annotation { "Feature Type Name" : "Feature", "Feature Type Description" : "" }
export const myFeature = defineFeature(function(context is Context, id is Id, definition is map)
    precondition{}
    {
        {
            var Q0;
            Q0=qCreatedBy(makeId("Front.planeOp"),FACE);
            var sketch = newSketch(context, id + "F0", { "sketchPlane" : qUnion([Q0])});
            skLineSegment(sketch, "E0", {"start": v(0, 0) * mm, "end": v(381, 0) * mm});
            skLineSegment(sketch, "E1", {"start": v(0, 0) * mm, "end": v(-381, 0) * mm});
            skLineSegment(sketch, "E2", {"start": v(0, 0) * mm, "end": v(0, 190.5) * mm, "construction": true});
            skLineSegment(sketch, "E3", {"start": v(-381, 0) * mm, "end": v(0, 190.5) * mm});
            skLineSegment(sketch, "E4", {"start": v(0, 190.5) * mm, "end": v(381, 0) * mm});
            skLineSegment(sketch, "E5", {"start": v(0, 190.5) * mm, "end": v(0, 228.6) * mm, "construction": true});
            skLineSegment(sketch, "E6", {"start": v(-381, 0) * mm, "end": v(-457.2, 0) * mm});
            skLineSegment(sketch, "E7", {"start": v(381, 0) * mm, "end": v(457.2, 0) * mm});
            skLineSegment(sketch, "E8", {"start": v(457.2, 0) * mm, "end": v(0, 228.6) * mm});
            skLineSegment(sketch, "E9", {"start": v(-457.2, 0) * mm, "end": v(0, 228.6) * mm});
            skLineSegment(sketch, "E10", {"start": v(-381, 0) * mm, "end": v(-381, -279.4) * mm});
            skLineSegment(sketch, "E11", {"start": v(381, 0) * mm, "end": v(381, -279.4) * mm});
            skLineSegment(sketch, "E12", {"start": v(381, -279.4) * mm, "end": v(-381, -279.4) * mm});
            skLineSegment(sketch, "E13", {"start": v(-381, -279.4) * mm, "end": v(-381, -330.2) * mm});
            skLineSegment(sketch, "E14", {"start": v(381, -279.4) * mm, "end": v(381, -330.2) * mm});
            skLineSegment(sketch, "E15", {"start": v(381, -330.2) * mm, "end": v(-381, -330.2) * mm});
            skLineSegment(sketch, "E16", {"start": v(-279.4, -279.4) * mm, "end": v(-279.4, -101.6) * mm});
            skLineSegment(sketch, "E17", {"start": v(-279.4, -101.6) * mm, "end": v(-203.2, -101.6) * mm});
            skLineSegment(sketch, "E18", {"start": v(-203.2, -101.6) * mm, "end": v(-203.2, -279.4) * mm});
            skLineSegment(sketch, "E19", {"start": v(-203.2, -279.4) * mm, "end": v(-279.4, -279.4) * mm});
            skLineSegment(sketch, "E20.0", {"start": v(-177.8, -76.2) * mm, "end": v(-177.8, -279.4) * mm});
            skLineSegment(sketch, "E20.1", {"start": v(-304.8, -76.2) * mm, "end": v(-177.8, -76.2) * mm});
            skLineSegment(sketch, "E20.2", {"start": v(-304.8, -279.4) * mm, "end": v(-304.8, -76.2) * mm});
            skLineSegment(sketch, "E21", {"start": v(-304.8, -279.4) * mm, "end": v(-279.4, -279.4) * mm});
            skLineSegment(sketch, "E22", {"start": v(-203.2, -279.4) * mm, "end": v(-177.8, -279.4) * mm});
            skLineSegment(sketch, "E23", {"start": v(381, -330.2) * mm, "end": v(762, -330.2) * mm});
            skLineSegment(sketch, "E24", {"start": v(381, -279.4) * mm, "end": v(762, -279.4) * mm});
            skLineSegment(sketch, "E25", {"start": v(762, -279.4) * mm, "end": v(762, -330.2) * mm});
            skLineSegment(sketch, "E26", {"start": v(762, -279.4) * mm, "end": v(762, -50.8) * mm});
            skLineSegment(sketch, "E27", {"start": v(381, 0) * mm, "end": v(762, -50.8) * mm});
            skLineSegment(sketch, "E28", {"start": v(762, -101.6) * mm, "end": v(381, -50.8) * mm});
            skLineSegment(sketch, "E29.bottom", {"start": v(50.8, -101.6) * mm, "end": v(279.4, -101.6) * mm});
            skLineSegment(sketch, "E29.top", {"start": v(50.8, -203.2) * mm, "end": v(279.4, -203.2) * mm});
            skLineSegment(sketch, "E29.left", {"start": v(50.8, -101.6) * mm, "end": v(50.8, -203.2) * mm});
            skLineSegment(sketch, "E29.right", {"start": v(279.4, -101.6) * mm, "end": v(279.4, -203.2) * mm});
            skLineSegment(sketch, "E30.0", {"start": v(38.1, -88.9) * mm, "end": v(292.1, -88.9) * mm});
            skLineSegment(sketch, "E30.1", {"start": v(38.1, -88.9) * mm, "end": v(38.1, -215.9) * mm});
            skLineSegment(sketch, "E30.2", {"start": v(38.1, -215.9) * mm, "end": v(292.1, -215.9) * mm});
            skLineSegment(sketch, "E30.3", {"start": v(292.1, -88.9) * mm, "end": v(292.1, -215.9) * mm});
            skLineSegment(sketch, "E31.bottom", {"start": v(508, -127) * mm, "end": v(596.9, -127) * mm});
            skLineSegment(sketch, "E31.top", {"start": v(508, -228.6) * mm, "end": v(596.9, -228.6) * mm});
            skLineSegment(sketch, "E31.left", {"start": v(508, -127) * mm, "end": v(508, -228.6) * mm});
            skLineSegment(sketch, "E31.right", {"start": v(596.9, -127) * mm, "end": v(596.9, -228.6) * mm});
            skLineSegment(sketch, "E32.0", {"start": v(495.3, -114.3) * mm, "end": v(609.6, -114.3) * mm});
            skLineSegment(sketch, "E32.1", {"start": v(495.3, -114.3) * mm, "end": v(495.3, -241.3) * mm});
            skLineSegment(sketch, "E32.2", {"start": v(495.3, -241.3) * mm, "end": v(609.6, -241.3) * mm});
            skLineSegment(sketch, "E32.3", {"start": v(609.6, -114.3) * mm, "end": v(609.6, -241.3) * mm});
            skText(sketch, "E33", { "text": "Property of\nLily Preston", "fontName": "OpenSans-Regular.ttf"});
            skLineSegment(sketch, "E34", {"start": v(246.7, 105.25) * mm, "end": v(246.7, 232.25) * mm});
            skLineSegment(sketch, "E35", {"start": v(246.7, 232.25) * mm, "end": v(170.5, 232.25) * mm});
            skLineSegment(sketch, "E36", {"start": v(170.5, 232.25) * mm, "end": v(170.5, 143.35) * mm});
            skLineSegment(sketch, "E37", {"start": v(170.5, 143.35) * mm, "end": v(246.7, 105.25) * mm});
            const initialGuessF0  = {"E33": [0.4505, 0.09872, 1, 0, 0.02776]};
            skSetInitialGuess(sketch, initialGuessF0);
            skSolve(sketch);
        }
        {
            var Q0;
            Q0=makeQuery(id+"F0.imprint","IMPRINT",FACE,{"disambiguationData":[TD([[makeQuery(id+"F0.imprint","IMPRINT",EDGE,{"derivedFrom":sQuery(id+"F0.wireOp",EDGE,"E3")}),1.0]])]});
            var Q1;
            {var subQ0=sQuery(id+"F0.wireOp",EDGE,"E27");Q1=makeQuery(id+"F0.imprint","IMPRINT",FACE,{"disambiguationData":[TD([[makeQuery(id+"F0.imprint","IMPRINT",EDGE,{"derivedFrom":subQ0}),-1.0]])]});}
            extrude(context, id + "F1", {"entities" : qUnion([Q0, Q1]), "depth" : 76.2 * mm, "offsetDistance" : 25.4 * mm, "hasSecondDirection" : true, "secondDirectionOppositeDirection" : true, "secondDirectionDepth" : 1016 * mm});
        }
        {
            var Q0;
            Q0=makeQuery(id+"F0.imprint","IMPRINT",FACE,{"disambiguationData":[TD([[makeQuery(id+"F0.imprint","IMPRINT",EDGE,{"derivedFrom":sQuery(id+"F0.wireOp",EDGE,"E0")}),1.0]])]});
            extrude(context, id + "F2", {"entities" : qUnion([Q0]), "operationType" : NewBodyOperationType.ADD, "depth" : 38.1 * mm, "offsetDistance" : 25.4 * mm, "hasSecondDirection" : true, "secondDirectionOppositeDirection" : true, "secondDirectionDepth" : 990.6 * mm});
        }
        {
            var Q0;
            {var subQ6=sQuery(id+"F0.wireOp",EDGE,"E0");Q0=makeQuery(id+"F0.imprint","IMPRINT",FACE,{"disambiguationData":[TD([[makeQuery(id+"F0.imprint","IMPRINT",EDGE,{"derivedFrom":subQ6}),-1.0]])]});}
            var Q1;
            {var subQ1=sQuery(id+"F0.wireOp",EDGE,"E24");Q1=makeQuery(id+"F0.imprint","IMPRINT",FACE,{"disambiguationData":[TD([[makeQuery(id+"F0.imprint","IMPRINT",EDGE,{"derivedFrom":subQ1}),1.0]])]});}
            extrude(context, id + "F3", {"entities" : qUnion([Q0, Q1]), "depth" : 38.1 * mm, "offsetDistance" : 25.4 * mm, "hasSecondDirection" : true, "secondDirectionOppositeDirection" : true, "secondDirectionDepth" : 990.6 * mm});
        }
        {
            var Q0;
            Q0=makeQuery(id+"F0.imprint","IMPRINT",FACE,{"disambiguationData":[TD([[makeQuery(id+"F0.imprint","IMPRINT",EDGE,{"derivedFrom":sQuery(id+"F0.wireOp",EDGE,"E16")}),1.0]])]});
            var Q1;
            Q1=makeQuery(id+"F0.imprint","IMPRINT",FACE,{"disambiguationData":[TD([[makeQuery(id+"F0.imprint","IMPRINT",EDGE,{"derivedFrom":sQuery(id+"F0.wireOp",EDGE,"E29.bottom")}),1.0]])]});
            var Q2;
            Q2=makeQuery(id+"F0.imprint","IMPRINT",FACE,{"disambiguationData":[TD([[makeQuery(id+"F0.imprint","IMPRINT",EDGE,{"derivedFrom":sQuery(id+"F0.wireOp",EDGE,"E31.bottom")}),1.0]])]});
            extrude(context, id + "F4", {"entities" : qUnion([Q0, Q1, Q2]), "operationType" : NewBodyOperationType.ADD, "depth" : 50.8 * mm, "offsetDistance" : 25.4 * mm, "hasSecondDirection" : true, "secondDirectionOppositeDirection" : true, "secondDirectionDepth" : 990.6 * mm});
        }
        {
            var Q0;
            Q0=makeQuery(id+"F0.imprint","IMPRINT",FACE,{"disambiguationData":[TD([[makeQuery(id+"F0.imprint","IMPRINT",EDGE,{"derivedFrom":sQuery(id+"F0.wireOp",EDGE,"E16")}),-1.0]])]});
            var Q1;
            Q1=makeQuery(id+"F0.imprint","IMPRINT",FACE,{"disambiguationData":[TD([[makeQuery(id+"F0.imprint","IMPRINT",EDGE,{"derivedFrom":sQuery(id+"F0.wireOp",EDGE,"E29.bottom")}),-1.0]])]});
            var Q2;
            Q2=makeQuery(id+"F0.imprint","IMPRINT",FACE,{"disambiguationData":[TD([[makeQuery(id+"F0.imprint","IMPRINT",EDGE,{"derivedFrom":sQuery(id+"F0.wireOp",EDGE,"E31.bottom")}),-1.0]])]});
            extrude(context, id + "F5", {"entities" : qUnion([Q0, Q1, Q2]), "operationType" : NewBodyOperationType.ADD, "depth" : 38.1 * mm, "offsetDistance" : 25.4 * mm, "hasSecondDirection" : true, "secondDirectionOppositeDirection" : true, "secondDirectionDepth" : 990.6 * mm});
        }
        {
            var Q0;
            {var subQ1=sQuery(id+"F0.wireOp",EDGE,"E13");Q0=makeQuery(id+"F0.imprint","IMPRINT",FACE,{"disambiguationData":[TD([[makeQuery(id+"F0.imprint","IMPRINT",EDGE,{"derivedFrom":subQ1}),1.0]])]});}
            var Q1;
            Q1=makeQuery(id+"F0.imprint","IMPRINT",FACE,{"disambiguationData":[TD([[makeQuery(id+"F0.imprint","IMPRINT",EDGE,{"derivedFrom":sQuery(id+"F0.wireOp",EDGE,"E14")}),1.0]])]});
            extrude(context, id + "F6", {"entities" : qUnion([Q0, Q1]), "operationType" : NewBodyOperationType.ADD, "depth" : 381 * mm, "offsetDistance" : 25.4 * mm, "hasSecondDirection" : true, "secondDirectionOppositeDirection" : true, "secondDirectionDepth" : 990.6 * mm});
        }
        {
            var Q0;
            Q0=makeQuery(id+"F6.opExtrude","CAP_EDGE",EDGE,{"disambiguationData":[OSD([sQuery(id+"F0.wireOp",EDGE,"E12"),sQuery(id+"F0.wireOp",EDGE,"E19"),sQuery(id+"F0.wireOp",EDGE,"E21"),sQuery(id+"F0.wireOp",EDGE,"E22"),sQuery(id+"F0.wireOp",EDGE,"E24")])],"isStart":false});
            fillet(context, id + "F7", {"entities" : qUnion([Q0]), "radius" : 76.2 * mm, "tangentPropagation" : true, "allowEdgeOverflow" : false});
        }
        {
            var Q0;
            Q0=makeQuery(id+"F6.opExtrude","SWEPT_FACE",FACE,{"disambiguationData":[OSD([sQuery(id+"F0.wireOp",EDGE,"E12"),sQuery(id+"F0.wireOp",EDGE,"E19"),sQuery(id+"F0.wireOp",EDGE,"E21"),sQuery(id+"F0.wireOp",EDGE,"E22"),sQuery(id+"F0.wireOp",EDGE,"E24")])]});
            var sketch = newSketch(context, id + "F8", { "sketchPlane" : qUnion([Q0])});
            skText(sketch, "E38", { "text": "Lily Preston\n", "fontName": "OpenSans-Regular.ttf"});
            const initialGuessF8  = {"E38": [-0.21851, -0.22048, 1, 0, 0.09562]};
            skSetInitialGuess(sketch, initialGuessF8);
            skSolve(sketch);
        }
        {
            var Q0;
            Q0 = qSketchRegion(id + "F8", true);
            extrude(context, id + "F9", {"entities" : qUnion([Q0]), "operationType" : NewBodyOperationType.ADD, "depth" : 12.7 * mm, "offsetDistance" : 25.4 * mm});
        }
        {
            var Q0;
            Q0=makeQuery(id+"F6.boolean.opBoolean","MERGE",FACE,{"derivedFrom":[makeQuery(id+"F3.opExtrude","SWEPT_FACE",FACE,{"disambiguationData":[OSD([sQuery(id+"F0.wireOp",EDGE,"E26")])]}),makeQuery(id+"F6.opExtrude","SWEPT_FACE",FACE,{"disambiguationData":[OSD([sQuery(id+"F0.wireOp",EDGE,"E25")])]})]});
            var sketch = newSketch(context, id + "F10", { "sketchPlane" : qUnion([Q0])});
            skLineSegment(sketch, "E39.bottom", {"start": v(139.7, -177.8) * mm, "end": v(266.7, -177.8) * mm});
            skLineSegment(sketch, "E39.top", {"start": v(139.7, -254) * mm, "end": v(266.7, -254) * mm});
            skLineSegment(sketch, "E39.left", {"start": v(139.7, -177.8) * mm, "end": v(139.7, -254) * mm});
            skLineSegment(sketch, "E39.right", {"start": v(266.7, -177.8) * mm, "end": v(266.7, -254) * mm});
            skLineSegment(sketch, "E40.0", {"start": v(114.3, -152.4) * mm, "end": v(292.1, -152.4) * mm});
            skLineSegment(sketch, "E40.1", {"start": v(114.3, -152.4) * mm, "end": v(114.3, -279.4) * mm});
            skLineSegment(sketch, "E40.2", {"start": v(114.3, -279.4) * mm, "end": v(292.1, -279.4) * mm});
            skLineSegment(sketch, "E40.3", {"start": v(292.1, -152.4) * mm, "end": v(292.1, -279.4) * mm});
            skLineSegment(sketch, "E41.bottom", {"start": v(685.8, -177.8) * mm, "end": v(812.8, -177.8) * mm});
            skLineSegment(sketch, "E41.top", {"start": v(685.8, -254) * mm, "end": v(812.8, -254) * mm});
            skLineSegment(sketch, "E41.left", {"start": v(685.8, -177.8) * mm, "end": v(685.8, -254) * mm});
            skLineSegment(sketch, "E41.right", {"start": v(812.8, -177.8) * mm, "end": v(812.8, -254) * mm});
            skLineSegment(sketch, "E42.0", {"start": v(660.4, -152.4) * mm, "end": v(838.2, -152.4) * mm});
            skLineSegment(sketch, "E42.1", {"start": v(660.4, -152.4) * mm, "end": v(660.4, -279.4) * mm});
            skLineSegment(sketch, "E42.2", {"start": v(660.4, -279.4) * mm, "end": v(838.2, -279.4) * mm});
            skLineSegment(sketch, "E42.3", {"start": v(838.2, -152.4) * mm, "end": v(838.2, -279.4) * mm});
            skSolve(sketch);
        }
        {
            var Q0;
            Q0=makeQuery(id+"F10.imprint","IMPRINT",FACE,{"disambiguationData":[TD([[makeQuery(id+"F10.imprint","IMPRINT",EDGE,{"derivedFrom":sQuery(id+"F10.wireOp",EDGE,"E39.bottom")}),1.0]])]});
            var Q1;
            Q1=makeQuery(id+"F10.imprint","IMPRINT",FACE,{"disambiguationData":[TD([[makeQuery(id+"F10.imprint","IMPRINT",EDGE,{"derivedFrom":sQuery(id+"F10.wireOp",EDGE,"E41.bottom")}),1.0]])]});
            extrude(context, id + "F11", {"entities" : qUnion([Q0, Q1]), "operationType" : NewBodyOperationType.ADD, "depth" : 20.32 * mm, "offsetDistance" : 25.4 * mm});
        }
        {
            var Q0;
            Q0=makeQuery(id+"F11.boolean.opBoolean","SPLIT",FACE,{"disambiguationData":[TD([makeQuery(id+"F11.opExtrude","SWEPT_FACE",FACE,{"disambiguationData":[OSD([sQuery(id+"F10.wireOp",EDGE,"E39.bottom")])]})])],"derivedFrom":makeQuery(id+"F6.boolean.opBoolean","MERGE",FACE,{"derivedFrom":[makeQuery(id+"F3.opExtrude","SWEPT_FACE",FACE,{"disambiguationData":[OSD([sQuery(id+"F0.wireOp",EDGE,"E26")])]}),makeQuery(id+"F6.opExtrude","SWEPT_FACE",FACE,{"disambiguationData":[OSD([sQuery(id+"F0.wireOp",EDGE,"E25")])]})]})});
            var Q1;
            Q1=makeQuery(id+"F11.boolean.opBoolean","SPLIT",FACE,{"disambiguationData":[TD([makeQuery(id+"F11.opExtrude","SWEPT_FACE",FACE,{"disambiguationData":[OSD([sQuery(id+"F10.wireOp",EDGE,"E41.bottom")])]})])],"derivedFrom":makeQuery(id+"F6.boolean.opBoolean","MERGE",FACE,{"derivedFrom":[makeQuery(id+"F3.opExtrude","SWEPT_FACE",FACE,{"disambiguationData":[OSD([sQuery(id+"F0.wireOp",EDGE,"E26")])]}),makeQuery(id+"F6.opExtrude","SWEPT_FACE",FACE,{"disambiguationData":[OSD([sQuery(id+"F0.wireOp",EDGE,"E25")])]})]})});
            extrude(context, id + "F12", {"entities" : qUnion([Q0, Q1]), "operationType" : NewBodyOperationType.ADD, "depth" : 12.7 * mm, "offsetDistance" : 25.4 * mm});
        }
        {
            var Q0;
            {var subQ0=sQuery(id+"F0.wireOp",EDGE,"E24");var subQ1=sQuery(id+"F0.wireOp",EDGE,"E22");var subQ2=sQuery(id+"F0.wireOp",EDGE,"E21");var subQ3=sQuery(id+"F0.wireOp",EDGE,"E19");var subQ4=sQuery(id+"F0.wireOp",EDGE,"E12");var subQ5=sQuery(id+"F0.wireOp",EDGE,"E31.right");var subQ6=sQuery(id+"F0.wireOp",EDGE,"E31.left");var subQ7=sQuery(id+"F0.wireOp",EDGE,"E31.top");var subQ8=sQuery(id+"F0.wireOp",EDGE,"E31.bottom");var subQ9=sQuery(id+"F0.wireOp",EDGE,"E29.right");var subQ10=sQuery(id+"F0.wireOp",EDGE,"E29.left");var subQ11=sQuery(id+"F0.wireOp",EDGE,"E29.top");var subQ12=sQuery(id+"F0.wireOp",EDGE,"E29.bottom");var subQ13=sQuery(id+"F0.wireOp",EDGE,"E18");var subQ14=sQuery(id+"F0.wireOp",EDGE,"E17");var subQ15=sQuery(id+"F0.wireOp",EDGE,"E16");var subQ16=sQuery(id+"F0.wireOp",EDGE,"E32.3");var subQ17=sQuery(id+"F0.wireOp",EDGE,"E32.2");var subQ18=sQuery(id+"F0.wireOp",EDGE,"E32.1");var subQ19=sQuery(id+"F0.wireOp",EDGE,"E32.0");var subQ20=sQuery(id+"F0.wireOp",EDGE,"E30.3");var subQ21=sQuery(id+"F0.wireOp",EDGE,"E30.2");var subQ22=sQuery(id+"F0.wireOp",EDGE,"E30.1");var subQ23=sQuery(id+"F0.wireOp",EDGE,"E30.0");var subQ24=sQuery(id+"F0.wireOp",EDGE,"E20.2");var subQ25=sQuery(id+"F0.wireOp",EDGE,"E20.1");var subQ26=sQuery(id+"F0.wireOp",EDGE,"E20.0");Q0=makeQuery(id+"F6.boolean.opBoolean","MERGE",FACE,{"derivedFrom":[makeQuery(id+"F5.boolean.opBoolean","MERGE",FACE,{"derivedFrom":[makeQuery(id+"F4.boolean.opBoolean","MERGE",FACE,{"derivedFrom":[makeQuery(id+"F3.opExtrude","CAP_FACE",FACE,{"disambiguationData":[OSD([sQuery(id+"F0.wireOp",EDGE,"E0"),sQuery(id+"F0.wireOp",EDGE,"E1"),sQuery(id+"F0.wireOp",EDGE,"E10"),sQuery(id+"F0.wireOp",EDGE,"E11"),subQ4,subQ26,subQ25,subQ24,subQ0,sQuery(id+"F0.wireOp",EDGE,"E26"),sQuery(id+"F0.wireOp",EDGE,"E28"),subQ23,subQ22,subQ21,subQ20,subQ19,subQ18,subQ17,subQ16])],"isStart":true}),makeQuery(id+"F4.opExtrude","CAP_FACE",FACE,{"disambiguationData":[OSD([subQ15,subQ14,subQ13,subQ26,subQ25,subQ24,subQ2,subQ1])],"isStart":true}),makeQuery(id+"F4.opExtrude","CAP_FACE",FACE,{"disambiguationData":[OSD([subQ12,subQ11,subQ10,subQ9,subQ23,subQ22,subQ21,subQ20])],"isStart":true}),makeQuery(id+"F4.opExtrude","CAP_FACE",FACE,{"disambiguationData":[OSD([subQ8,subQ7,subQ6,subQ5,subQ19,subQ18,subQ17,subQ16])],"isStart":true})]}),makeQuery(id+"F5.opExtrude","CAP_FACE",FACE,{"disambiguationData":[OSD([subQ15,subQ14,subQ13,subQ3])],"isStart":true}),makeQuery(id+"F5.opExtrude","CAP_FACE",FACE,{"disambiguationData":[OSD([subQ12,subQ11,subQ10,subQ9])],"isStart":true}),makeQuery(id+"F5.opExtrude","CAP_FACE",FACE,{"disambiguationData":[OSD([subQ8,subQ7,subQ6,subQ5])],"isStart":true})]}),makeQuery(id+"F6.opExtrude","CAP_FACE",FACE,{"disambiguationData":[OSD([subQ4,sQuery(id+"F0.wireOp",EDGE,"E13"),sQuery(id+"F0.wireOp",EDGE,"E15"),subQ3,subQ2,subQ1,sQuery(id+"F0.wireOp",EDGE,"E23"),subQ0,sQuery(id+"F0.wireOp",EDGE,"E25")])],"isStart":true})]});}
            var sketch = newSketch(context, id + "F13", { "sketchPlane" : qUnion([Q0])});
            skLineSegment(sketch, "E43.bottom", {"start": v(-635, -127.67) * mm, "end": v(-381, -127.67) * mm});
            skLineSegment(sketch, "E43.top", {"start": v(-635, -254.67) * mm, "end": v(-381, -254.67) * mm});
            skLineSegment(sketch, "E43.left", {"start": v(-635, -127.67) * mm, "end": v(-635, -254.67) * mm});
            skLineSegment(sketch, "E43.right", {"start": v(-381, -127.67) * mm, "end": v(-381, -254.67) * mm});
            skLineSegment(sketch, "E44.0", {"start": v(-655.32, -107.35) * mm, "end": v(-360.68, -107.35) * mm});
            skLineSegment(sketch, "E44.1", {"start": v(-655.32, -107.35) * mm, "end": v(-655.32, -275) * mm});
            skLineSegment(sketch, "E44.2", {"start": v(-655.32, -275) * mm, "end": v(-360.68, -275) * mm});
            skLineSegment(sketch, "E44.3", {"start": v(-360.68, -107.35) * mm, "end": v(-360.68, -275) * mm});
            skSolve(sketch);
        }
        {
            var Q0;
            Q0=makeQuery(id+"F13.imprint","IMPRINT",FACE,{"disambiguationData":[TD([[makeQuery(id+"F13.imprint","IMPRINT",EDGE,{"derivedFrom":sQuery(id+"F13.wireOp",EDGE,"E43.bottom")}),1.0]])]});
            extrude(context, id + "F14", {"entities" : qUnion([Q0]), "operationType" : NewBodyOperationType.ADD, "depth" : 20.32 * mm, "offsetDistance" : 25.4 * mm});
        }
        {
            var Q0;
            {var subQ0=sQuery(id+"F0.wireOp",EDGE,"E24");var subQ1=sQuery(id+"F0.wireOp",EDGE,"E22");var subQ2=sQuery(id+"F0.wireOp",EDGE,"E21");var subQ3=sQuery(id+"F0.wireOp",EDGE,"E19");var subQ4=sQuery(id+"F0.wireOp",EDGE,"E12");var subQ5=sQuery(id+"F0.wireOp",EDGE,"E31.right");var subQ6=sQuery(id+"F0.wireOp",EDGE,"E31.left");var subQ7=sQuery(id+"F0.wireOp",EDGE,"E31.top");var subQ8=sQuery(id+"F0.wireOp",EDGE,"E31.bottom");var subQ9=sQuery(id+"F0.wireOp",EDGE,"E29.right");var subQ10=sQuery(id+"F0.wireOp",EDGE,"E29.left");var subQ11=sQuery(id+"F0.wireOp",EDGE,"E29.top");var subQ12=sQuery(id+"F0.wireOp",EDGE,"E29.bottom");var subQ13=sQuery(id+"F0.wireOp",EDGE,"E18");var subQ14=sQuery(id+"F0.wireOp",EDGE,"E17");var subQ15=sQuery(id+"F0.wireOp",EDGE,"E16");var subQ16=sQuery(id+"F0.wireOp",EDGE,"E32.3");var subQ17=sQuery(id+"F0.wireOp",EDGE,"E32.2");var subQ18=sQuery(id+"F0.wireOp",EDGE,"E32.1");var subQ19=sQuery(id+"F0.wireOp",EDGE,"E32.0");var subQ20=sQuery(id+"F0.wireOp",EDGE,"E30.3");var subQ21=sQuery(id+"F0.wireOp",EDGE,"E30.2");var subQ22=sQuery(id+"F0.wireOp",EDGE,"E30.1");var subQ23=sQuery(id+"F0.wireOp",EDGE,"E30.0");var subQ24=sQuery(id+"F0.wireOp",EDGE,"E20.2");var subQ25=sQuery(id+"F0.wireOp",EDGE,"E20.1");var subQ26=sQuery(id+"F0.wireOp",EDGE,"E20.0");Q0=makeQuery(id+"F14.boolean.opBoolean","SPLIT",FACE,{"disambiguationData":[TD([makeQuery(id+"F14.opExtrude","SWEPT_FACE",FACE,{"disambiguationData":[OSD([sQuery(id+"F13.wireOp",EDGE,"E43.bottom")])]})])],"derivedFrom":makeQuery(id+"F6.boolean.opBoolean","MERGE",FACE,{"derivedFrom":[makeQuery(id+"F5.boolean.opBoolean","MERGE",FACE,{"derivedFrom":[makeQuery(id+"F4.boolean.opBoolean","MERGE",FACE,{"derivedFrom":[makeQuery(id+"F3.opExtrude","CAP_FACE",FACE,{"disambiguationData":[OSD([sQuery(id+"F0.wireOp",EDGE,"E0"),sQuery(id+"F0.wireOp",EDGE,"E1"),sQuery(id+"F0.wireOp",EDGE,"E10"),sQuery(id+"F0.wireOp",EDGE,"E11"),subQ4,subQ26,subQ25,subQ24,subQ0,sQuery(id+"F0.wireOp",EDGE,"E26"),sQuery(id+"F0.wireOp",EDGE,"E28"),subQ23,subQ22,subQ21,subQ20,subQ19,subQ18,subQ17,subQ16])],"isStart":true}),makeQuery(id+"F4.opExtrude","CAP_FACE",FACE,{"disambiguationData":[OSD([subQ15,subQ14,subQ13,subQ26,subQ25,subQ24,subQ2,subQ1])],"isStart":true}),makeQuery(id+"F4.opExtrude","CAP_FACE",FACE,{"disambiguationData":[OSD([subQ12,subQ11,subQ10,subQ9,subQ23,subQ22,subQ21,subQ20])],"isStart":true}),makeQuery(id+"F4.opExtrude","CAP_FACE",FACE,{"disambiguationData":[OSD([subQ8,subQ7,subQ6,subQ5,subQ19,subQ18,subQ17,subQ16])],"isStart":true})]}),makeQuery(id+"F5.opExtrude","CAP_FACE",FACE,{"disambiguationData":[OSD([subQ15,subQ14,subQ13,subQ3])],"isStart":true}),makeQuery(id+"F5.opExtrude","CAP_FACE",FACE,{"disambiguationData":[OSD([subQ12,subQ11,subQ10,subQ9])],"isStart":true}),makeQuery(id+"F5.opExtrude","CAP_FACE",FACE,{"disambiguationData":[OSD([subQ8,subQ7,subQ6,subQ5])],"isStart":true})]}),makeQuery(id+"F6.opExtrude","CAP_FACE",FACE,{"disambiguationData":[OSD([subQ4,sQuery(id+"F0.wireOp",EDGE,"E13"),sQuery(id+"F0.wireOp",EDGE,"E15"),subQ3,subQ2,subQ1,sQuery(id+"F0.wireOp",EDGE,"E23"),subQ0,sQuery(id+"F0.wireOp",EDGE,"E25")])],"isStart":true})]})});}
            extrude(context, id + "F15", {"entities" : qUnion([Q0]), "operationType" : NewBodyOperationType.ADD, "depth" : 12.7 * mm, "offsetDistance" : 25.4 * mm});
        }
        {
            var Q0;
            Q0=makeQuery(id+"F1.opExtrude","SWEPT_FACE",FACE,{"disambiguationData":[OSD([sQuery(id+"F0.wireOp",EDGE,"E8")])]});
            var sketch = newSketch(context, id + "F16", { "sketchPlane" : qUnion([Q0])});
            skLineSegment(sketch, "E45.bottom", {"start": v(0, 111.4) * mm, "end": v(228.6, 111.4) * mm});
            skLineSegment(sketch, "E45.top", {"start": v(0, 238.4) * mm, "end": v(228.6, 238.4) * mm});
            skLineSegment(sketch, "E45.left", {"start": v(0, 111.4) * mm, "end": v(0, 238.4) * mm});
            skLineSegment(sketch, "E45.right", {"start": v(228.6, 111.4) * mm, "end": v(228.6, 238.4) * mm});
            skLineSegment(sketch, "E46.0", {"start": v(-12.7, 98.7) * mm, "end": v(-12.7, 251.1) * mm});
            skLineSegment(sketch, "E46.1", {"start": v(-12.7, 98.7) * mm, "end": v(241.3, 98.7) * mm});
            skLineSegment(sketch, "E46.2", {"start": v(241.3, 98.7) * mm, "end": v(241.3, 251.1) * mm});
            skLineSegment(sketch, "E46.3", {"start": v(-12.7, 251.1) * mm, "end": v(241.3, 251.1) * mm});
            skLineSegment(sketch, "E47.bottom", {"start": v(0, 304.9) * mm, "end": v(228.6, 304.9) * mm});
            skLineSegment(sketch, "E47.top", {"start": v(0, 431.9) * mm, "end": v(228.6, 431.9) * mm});
            skLineSegment(sketch, "E47.left", {"start": v(0, 304.9) * mm, "end": v(0, 431.9) * mm});
            skLineSegment(sketch, "E47.right", {"start": v(228.6, 304.9) * mm, "end": v(228.6, 431.9) * mm});
            skLineSegment(sketch, "E48.0", {"start": v(-12.7, 292.2) * mm, "end": v(-12.7, 444.6) * mm});
            skLineSegment(sketch, "E48.1", {"start": v(-12.7, 292.2) * mm, "end": v(241.3, 292.2) * mm});
            skLineSegment(sketch, "E48.2", {"start": v(241.3, 292.2) * mm, "end": v(241.3, 444.6) * mm});
            skLineSegment(sketch, "E48.3", {"start": v(-12.7, 444.6) * mm, "end": v(241.3, 444.6) * mm});
            skSolve(sketch);
        }
        {
            var Q0;
            Q0=makeQuery(id+"F16.imprint","IMPRINT",FACE,{"disambiguationData":[TD([[makeQuery(id+"F16.imprint","IMPRINT",EDGE,{"derivedFrom":sQuery(id+"F16.wireOp",EDGE,"E45.bottom")}),-1.0]])]});
            var Q1;
            Q1=makeQuery(id+"F16.imprint","IMPRINT",FACE,{"disambiguationData":[TD([[makeQuery(id+"F16.imprint","IMPRINT",EDGE,{"derivedFrom":sQuery(id+"F16.wireOp",EDGE,"E47.bottom")}),-1.0]])]});
            extrude(context, id + "F17", {"entities" : qUnion([Q0, Q1]), "operationType" : NewBodyOperationType.ADD, "depth" : 12.7 * mm, "offsetDistance" : 25.4 * mm});
        }
    });